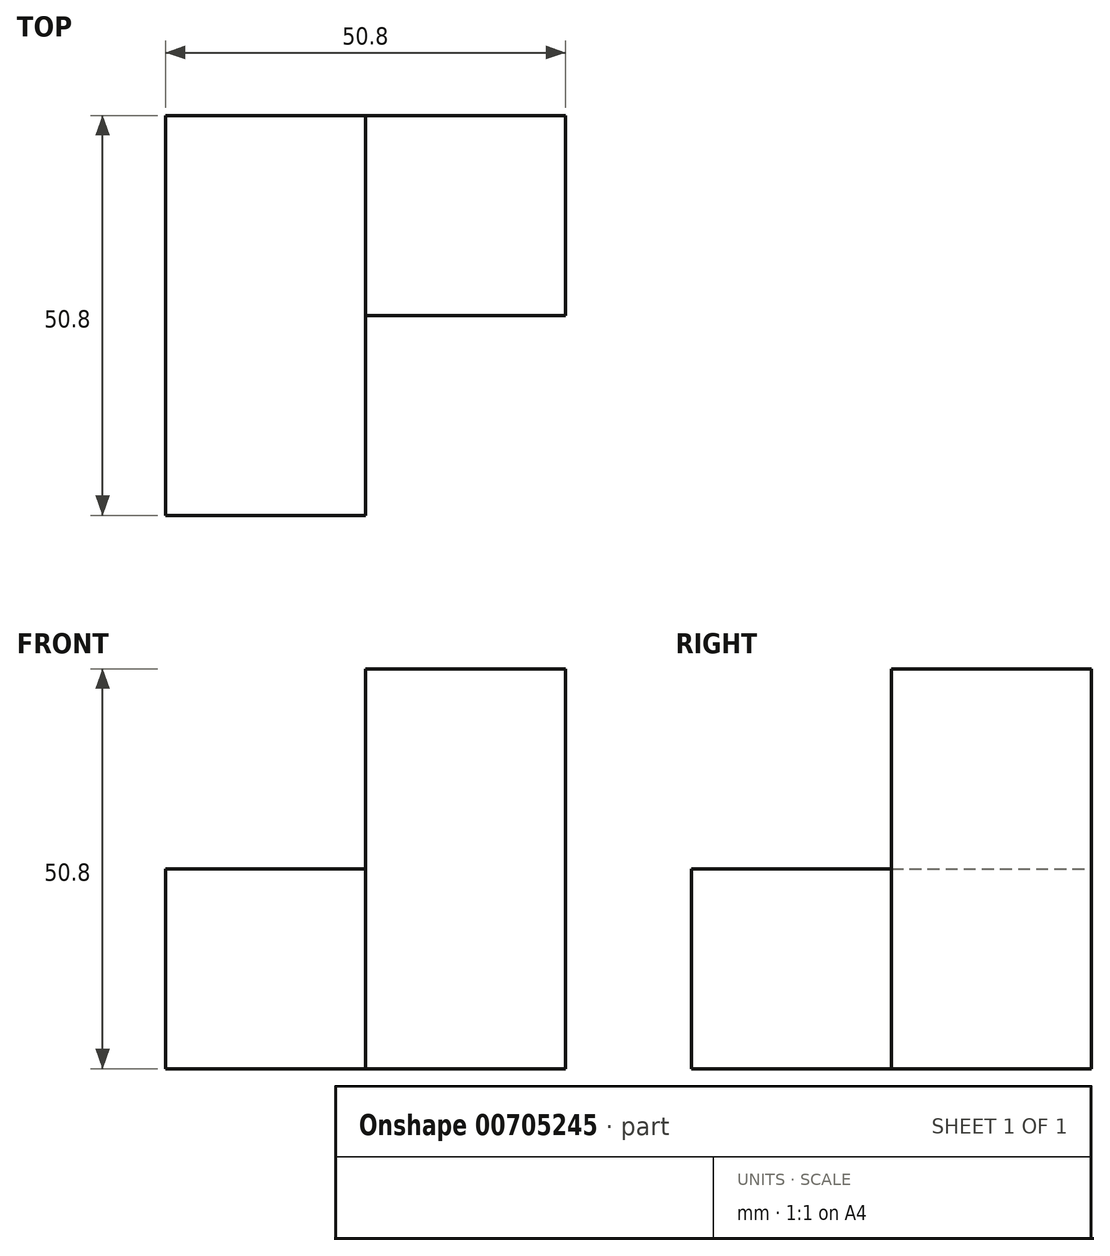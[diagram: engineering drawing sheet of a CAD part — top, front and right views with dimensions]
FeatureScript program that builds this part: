
annotation { "Feature Type Name" : "Feature", "Feature Type Description" : "" }
export const myFeature = defineFeature(function(context is Context, id is Id, definition is map)
    precondition{}
    {
        {
            var Q0;
            Q0=qCreatedBy(makeId("Front.planeOp"),FACE);
            var sketch = newSketch(context, id + "F0", { "sketchPlane" : qUnion([Q0])});
            skLineSegment(sketch, "E0.bottom", {"start": v(-25.4, 25.4) * mm, "end": v(0, 25.4) * mm});
            skLineSegment(sketch, "E0.top", {"start": v(-25.4, 0) * mm, "end": v(0, 0) * mm});
            skLineSegment(sketch, "E0.left", {"start": v(-25.4, 25.4) * mm, "end": v(-25.4, 0) * mm});
            skLineSegment(sketch, "E0.right", {"start": v(0, 25.4) * mm, "end": v(0, 0) * mm});
            skLineSegment(sketch, "E1.bottom", {"start": v(0, 25.4) * mm, "end": v(25.4, 25.4) * mm});
            skLineSegment(sketch, "E1.top", {"start": v(0, 0) * mm, "end": v(25.4, 0) * mm});
            skLineSegment(sketch, "E1.right", {"start": v(25.4, 25.4) * mm, "end": v(25.4, 0) * mm});
            skLineSegment(sketch, "E2.top", {"start": v(0, 50.8) * mm, "end": v(25.4, 50.8) * mm});
            skLineSegment(sketch, "E2.left", {"start": v(0, 25.4) * mm, "end": v(0, 50.8) * mm});
            skLineSegment(sketch, "E2.right", {"start": v(25.4, 25.4) * mm, "end": v(25.4, 50.8) * mm});
            skSolve(sketch);
        }
        {
            var Q0;
            Q0=makeQuery(id+"F0.imprint","IMPRINT",FACE,{"disambiguationData":[TD([[makeQuery(id+"F0.imprint","IMPRINT",EDGE,{"derivedFrom":sQuery(id+"F0.wireOp",EDGE,"E0.top")}),1.0]])]});
            extrude(context, id + "F1", {"entities" : qUnion([Q0]), "depth" : 50.8 * mm, "offsetDistance" : 25.4 * mm});
        }
        {
            var Q0;
            Q0=makeQuery(id+"F0.imprint","IMPRINT",FACE,{"disambiguationData":[TD([[makeQuery(id+"F0.imprint","IMPRINT",EDGE,{"derivedFrom":sQuery(id+"F0.wireOp",EDGE,"E1.bottom")}),1.0]])]});
            var Q1;
            Q1=makeQuery(id+"F0.imprint","IMPRINT",FACE,{"disambiguationData":[TD([[makeQuery(id+"F0.imprint","IMPRINT",EDGE,{"derivedFrom":sQuery(id+"F0.wireOp",EDGE,"E1.top")}),1.0]])]});
            extrude(context, id + "F2", {"entities" : qUnion([Q0, Q1]), "operationType" : NewBodyOperationType.ADD, "depth" : 25.4 * mm, "offsetDistance" : 25.4 * mm});
        }
    });
